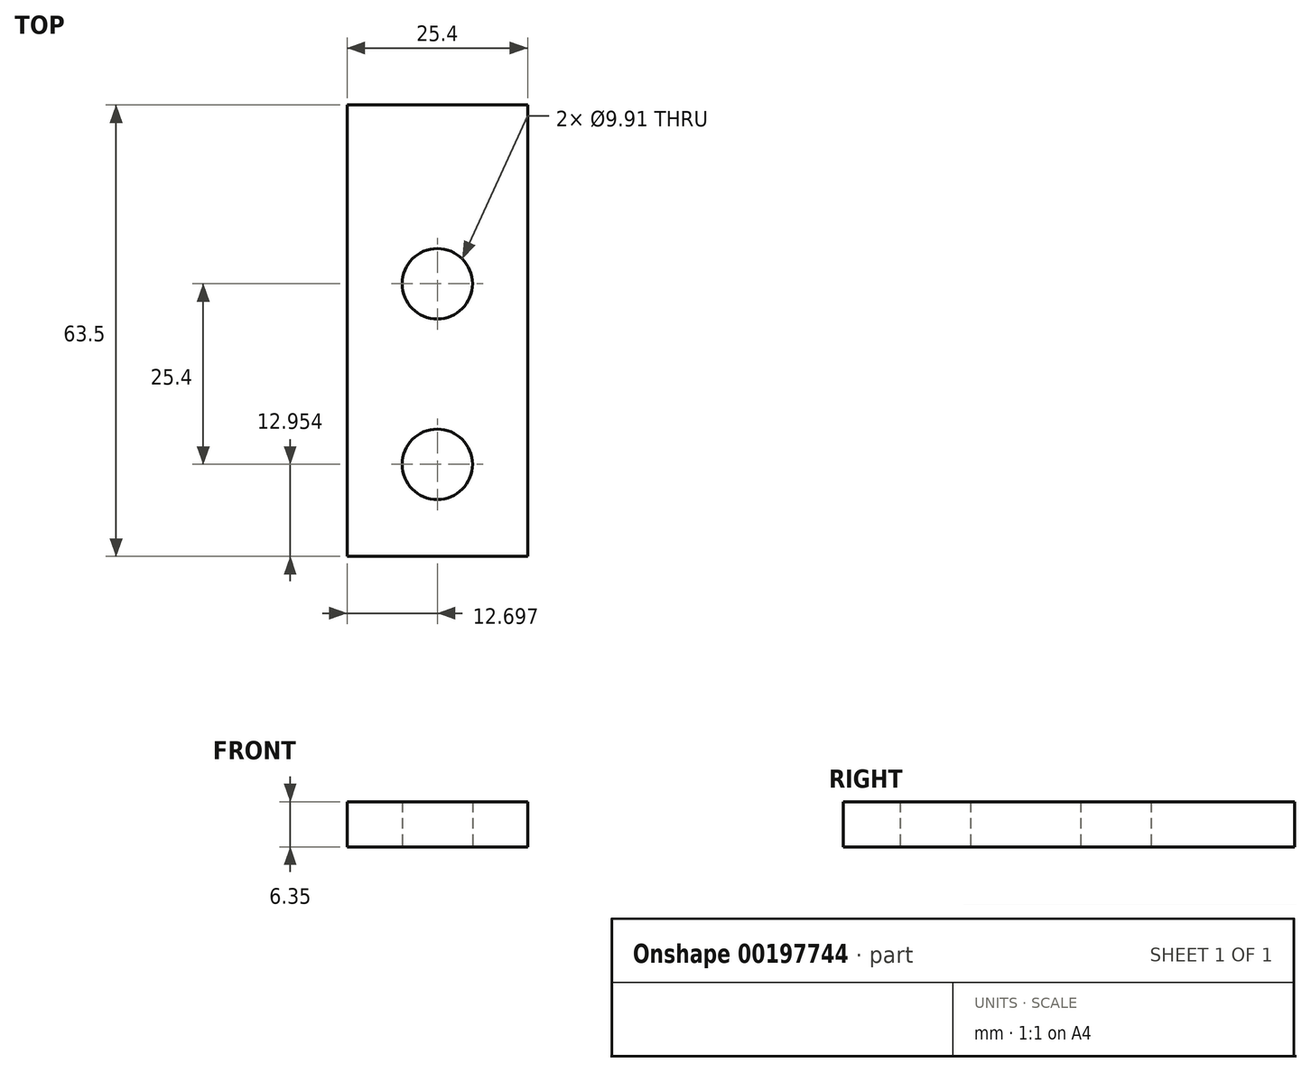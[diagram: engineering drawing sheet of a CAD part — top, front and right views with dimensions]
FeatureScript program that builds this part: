
annotation { "Feature Type Name" : "Feature", "Feature Type Description" : "" }
export const myFeature = defineFeature(function(context is Context, id is Id, definition is map)
    precondition{}
    {
        {
            var Q0;
            Q0=qCreatedBy(makeId("Top.planeOp"),FACE);
            var sketch = newSketch(context, id + "F0", { "sketchPlane" : qUnion([Q0])});
            skLineSegment(sketch, "E0.bottom", {"start": v(-111.44, -63.5) * mm, "end": v(-86.04, -63.5) * mm});
            skLineSegment(sketch, "E0.top", {"start": v(-111.44, 0) * mm, "end": v(-86.04, 0) * mm});
            skLineSegment(sketch, "E0.left", {"start": v(-111.44, -63.5) * mm, "end": v(-111.44, 0) * mm});
            skLineSegment(sketch, "E0.right", {"start": v(-86.04, -63.5) * mm, "end": v(-86.04, 0) * mm});
            skCircle(sketch, "E1", {"center": v(-98.74, -25.15) * mm, "radius": 4.95 * mm});
            skCircle(sketch, "E2", {"center": v(-98.74, -50.55) * mm, "radius": 4.95 * mm});
            skSolve(sketch);
        }
        {
            var Q0;
            Q0 = qSketchRegion(id + "F0", true);
            extrude(context, id + "F1", {"entities" : qUnion([Q0]), "depth" : 6.35 * mm});
        }
    });
